# Revit family: Shower-Slidebar-KOHLER-Awaken-K-98343
name_source: partatom
category: Specialty Equipment
revit_build: Autodesk Revit 2015 (Build: 20140606_1530(x64)
units: mm (PartAtom-declared; Revit-internal decimal feet)

## types (3) — shared parameters
ADA Compliant = Yes
Assembly Code = C1030200
Date Modified = 04/02/2019
Default Elevation = 72"
Description = Deluxe Slidebar, 36 Inch
Height = 41 5/8"
Length = 2 15/16"
Manufacturer = KOHLER Co.
MasterFormat 1995 = 10820
MasterFormat 2004 = 10.28.13
Material = Metal Construction
Product Documentation Link = https://www.us.kohler.com
Product Name = Awaken
Product Page URL = http://www.us.kohler.com
URL = https://www.us.kohler.com
WaterSense Certified = No
Width = 3 1/4"

## per-type parameters (varying)
| type | Finish | Model | Type |
| CP- Polished Chrome | Kohler-Metal-CP-Polished_Chrome | K-98343-CP | 1 |
| BN- Vibrant Brushed Nickel | Kohler-Metal-BN-Vibrant_Brushed_Nickel | K-98343-BN | 2 |
| 2BZ- Oil Rubbed Bronze | Kohler-Metal-2BZ-Oil_Rubbed_Bronze | K-98343-2BZ | 3 |

## geometry (parser evidence)
native form markers: Sweep x5
no freeform markers — native parametric forms only
